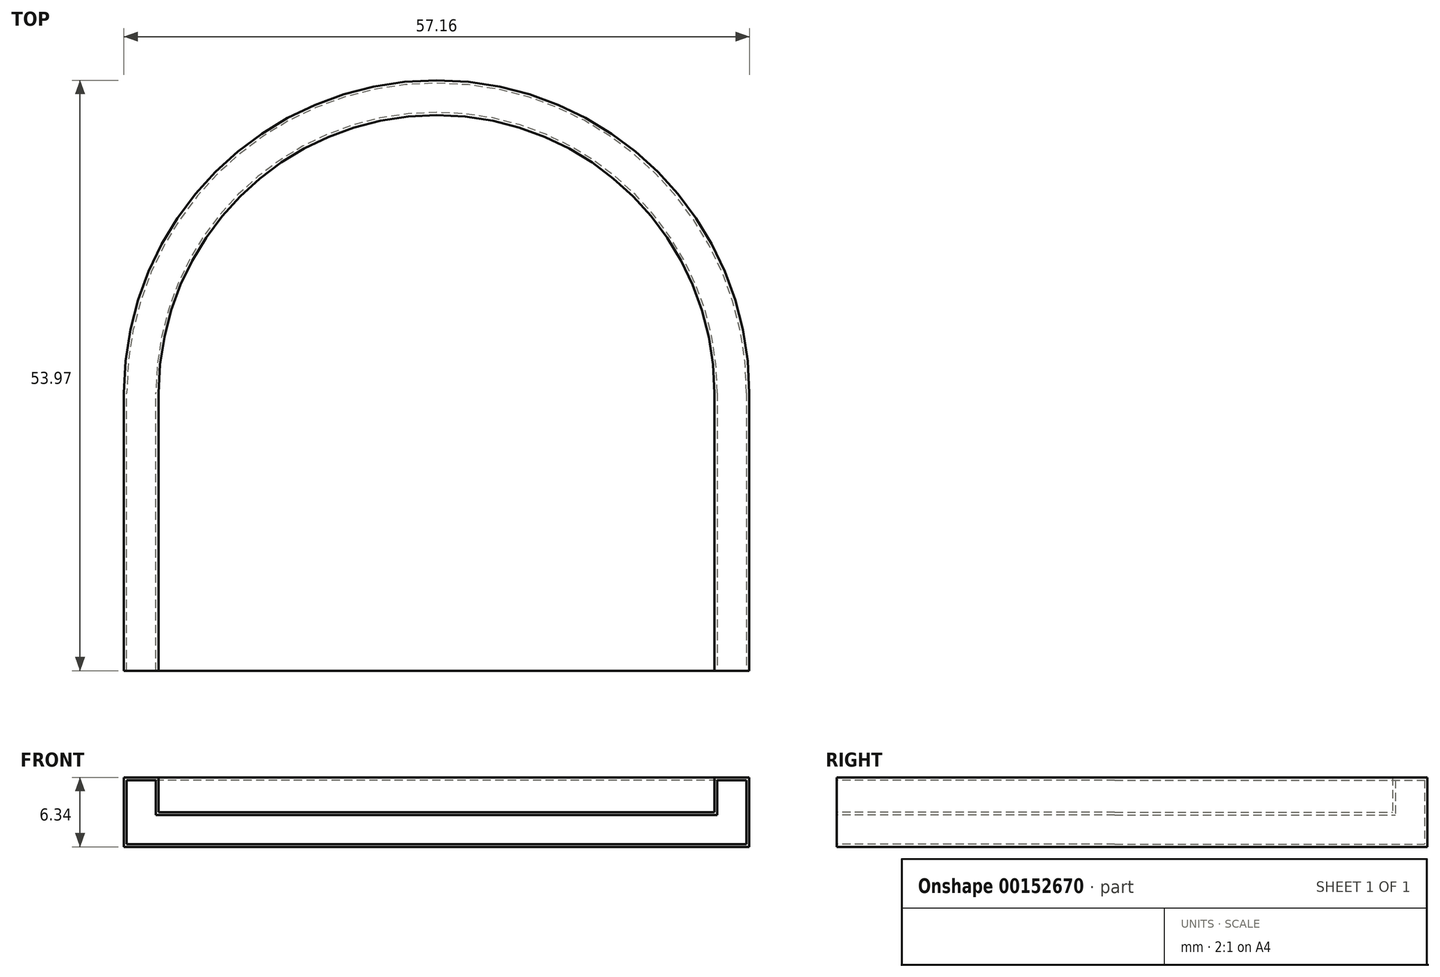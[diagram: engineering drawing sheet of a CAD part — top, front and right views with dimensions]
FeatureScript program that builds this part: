
annotation { "Feature Type Name" : "Feature", "Feature Type Description" : "" }
export const myFeature = defineFeature(function(context is Context, id is Id, definition is map)
    precondition{}
    {
        {
            var Q0;
            Q0=qCreatedBy(makeId("Top.planeOp"),FACE);
            var sketch = newSketch(context, id + "F0", { "sketchPlane" : qUnion([Q0])});
            skLineSegment(sketch, "E0.bottom", {"start": v(0, 0) * mm, "end": v(-3.18, 0) * mm});
            skLineSegment(sketch, "E0.top", {"start": v(0, 25.4) * mm, "end": v(-3.18, 25.4) * mm, "construction": true});
            skLineSegment(sketch, "E0.left", {"start": v(0, 0) * mm, "end": v(0, 25.4) * mm});
            skLineSegment(sketch, "E0.right", {"start": v(-3.17, 0) * mm, "end": v(-3.18, 25.4) * mm});
            skLineSegment(sketch, "E1", {"start": v(0, 25.4) * mm, "end": v(50.8, 25.4) * mm, "construction": true});
            skLineSegment(sketch, "E2.bottom", {"start": v(50.8, 25.4) * mm, "end": v(53.97, 25.4) * mm, "construction": true});
            skLineSegment(sketch, "E2.top", {"start": v(50.8, 0) * mm, "end": v(53.98, 0) * mm});
            skLineSegment(sketch, "E2.left", {"start": v(50.8, 25.4) * mm, "end": v(50.8, 0) * mm});
            skLineSegment(sketch, "E2.right", {"start": v(53.98, 25.4) * mm, "end": v(53.98, 0) * mm});
            skArc(sketch, "E3", {"start": v(50.8, 25.4) * mm, "mid": v(25.4, 50.8) * mm, "end": v(0, 25.4) * mm});
            skArc(sketch, "E4", {"start": v(53.98, 25.4) * mm, "mid": v(25.4, 53.98) * mm, "end": v(-3.18, 25.4) * mm});
            skSolve(sketch);
        }
        {
            var Q0;
            Q0 = qSketchRegion(id + "F0", true);
            extrude(context, id + "F1", {"entities" : qUnion([Q0]), "depth" : 3.17 * mm});
        }
        {
            var Q0;
            Q0=makeQuery(id+"F1.opExtrude","CAP_FACE",FACE,{"disambiguationData":[OSD([sQuery(id+"F0.wireOp",EDGE,"E0.bottom"),sQuery(id+"F0.wireOp",EDGE,"E0.left"),sQuery(id+"F0.wireOp",EDGE,"E0.right"),sQuery(id+"F0.wireOp",EDGE,"E2.top"),sQuery(id+"F0.wireOp",EDGE,"E2.left"),sQuery(id+"F0.wireOp",EDGE,"E2.right"),sQuery(id+"F0.wireOp",EDGE,"E3"),sQuery(id+"F0.wireOp",EDGE,"E4")])],"isStart":true});
            var sketch = newSketch(context, id + "F2", { "sketchPlane" : qUnion([Q0])});
            skLineSegment(sketch, "E5.bottom", {"start": v(53.98, 0) * mm, "end": v(-3.18, 0) * mm});
            skLineSegment(sketch, "E5.top", {"start": v(53.98, -25.4) * mm, "end": v(-3.18, -25.4) * mm, "construction": true});
            skLineSegment(sketch, "E5.left", {"start": v(53.98, 0) * mm, "end": v(53.98, -25.4) * mm});
            skLineSegment(sketch, "E5.right", {"start": v(-3.18, 0) * mm, "end": v(-3.18, -25.4) * mm});
            skArc(sketch, "E6", {"start": v(-3.18, -25.4) * mm, "mid": v(25.4, -53.98) * mm, "end": v(53.98, -25.4) * mm});
            skSolve(sketch);
        }
        {
            var Q0;
            Q0 = qSketchRegion(id + "F2", true);
            extrude(context, id + "F3", {"entities" : qUnion([Q0]), "operationType" : NewBodyOperationType.ADD, "depth" : 3.17 * mm});
        }
        {
            var Q0;
            Q0=makeQuery(id+"F3.boolean.opBoolean","MERGE",FACE,{"derivedFrom":[makeQuery(id+"F1.opExtrude","SWEPT_FACE",FACE,{"disambiguationData":[OSD([sQuery(id+"F0.wireOp",EDGE,"E0.bottom")])]}),makeQuery(id+"F1.opExtrude","SWEPT_FACE",FACE,{"disambiguationData":[OSD([sQuery(id+"F0.wireOp",EDGE,"E2.top")])]}),makeQuery(id+"F3.opExtrude","SWEPT_FACE",FACE,{"disambiguationData":[OSD([sQuery(id+"F2.wireOp",EDGE,"E5.bottom")])]})]});
            shell(context, id + "F4", {"entities" : qUnion([Q0]), "thickness" : 0.25 * mm});
        }
    });
